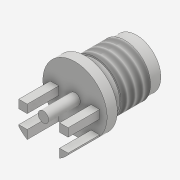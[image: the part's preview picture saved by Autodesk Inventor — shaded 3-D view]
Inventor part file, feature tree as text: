
AUTODESK INVENTOR PART (.ipt)
format: ipt  version: 2018 (Build 220112000, 112)  size: 155,648 bytes
history: native  units: mm
features: extrude x6, sketch x6, projected_geometry x2, plane x1, thread x1
ambient origin geometry x8: Origin, YZ Plane, XZ Plane, XY Plane, X Axis, Y Axis, Z Axis, Center Point
bodies: Solid1 (feature_tree)
feature tree (16):
  extrude  "Extrusion1"  Depth=6.35mm TaperAngle=0.0deg
  extrude  "Extrusion2"  Depth=1.26mm TaperAngle=0.0deg
  extrude  "Extrusion3"  Depth=3.9mm TaperAngle=0.0deg
  extrude  "Extrusion4"  Depth=6.1mm
  extrude  "Extrusion5"  Depth=1.7mm
  plane  "Work Plane1"
  extrude  "Extrusion6"  Depth=1.25mm
  thread  "Thread1"  [1 undecoded]
  sketch  "Sketch1"  dims[d0=6.0mm d1=6.35mm d2=0.0mm]
  sketch  "Sketch2"  dims[d3=7.93mm d4=1.26mm d5=0.0mm]
  sketch  "Sketch3"  dims[d6=1.3mm d7=3.9mm d8=0.0mm]
  sketch  "Sketch4"  dims[d11=4.0mm d12=6.1mm]
  sketch  "Sketch5"  dims[d13=3.9mm d14=0.0mm d15=1.7mm]
  projected_geometry  "Projected Loop1"
  projected_geometry  "Projected Loop2"
  sketch  "Sketch6"  dims[d16=3.9mm d17=0.0mm d18=1.25mm d19=6.35mm d20=3.65mm d21=0.0mm d22=10.0mm d23=0.0mm]
note: 1 required parameter value undecoded (feature->parameter linkage not recoverable at this tier; creation-order binding heuristic only, values carry confidence <= 0.55)
